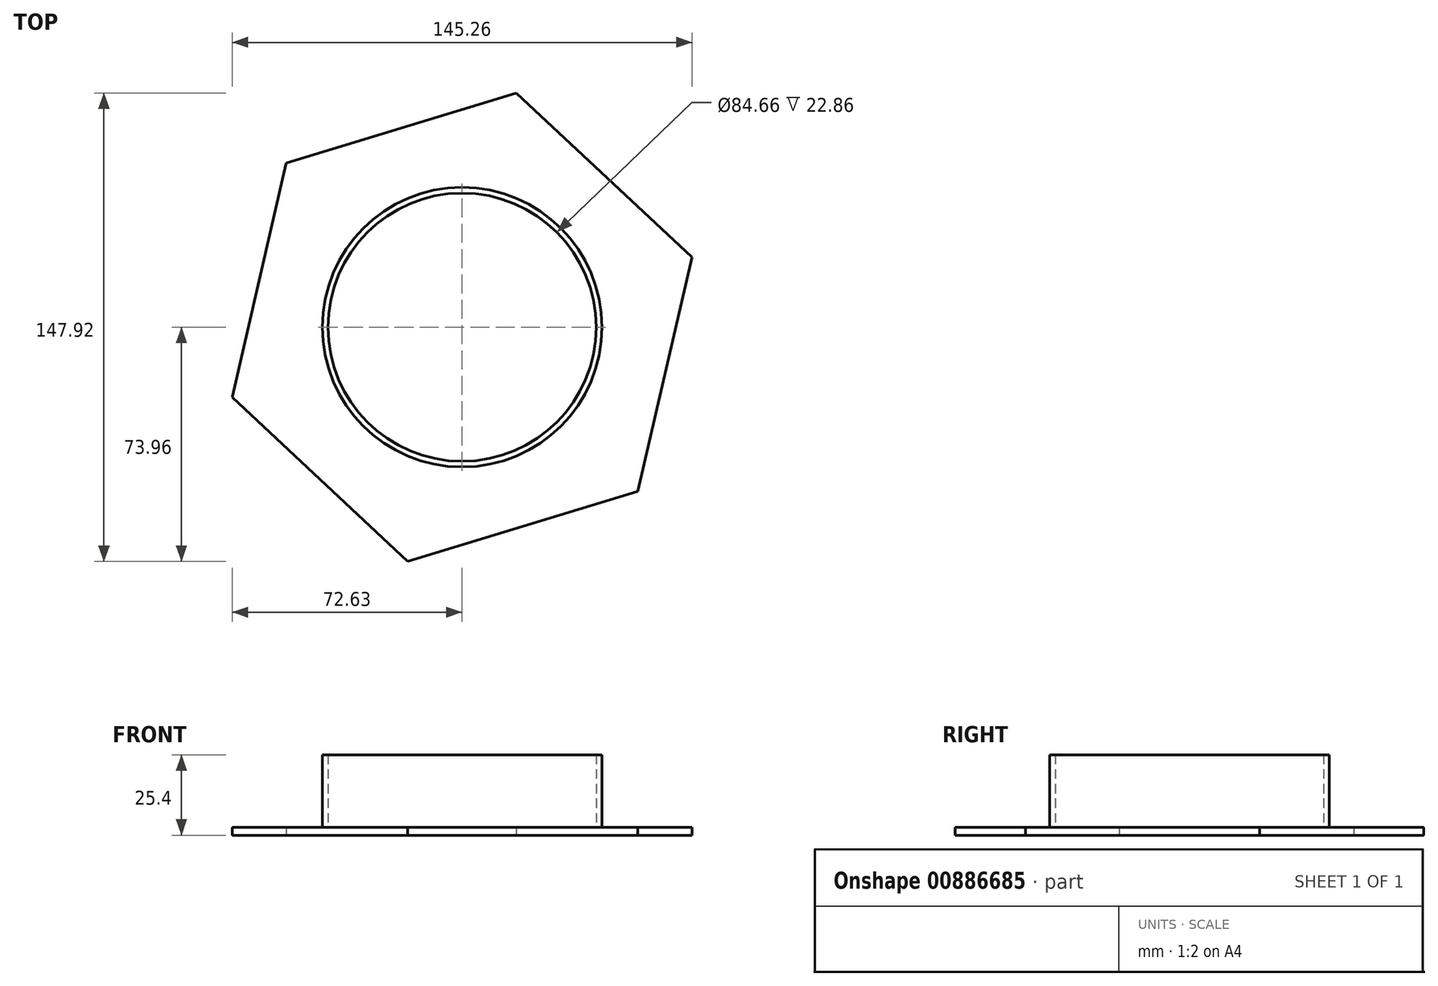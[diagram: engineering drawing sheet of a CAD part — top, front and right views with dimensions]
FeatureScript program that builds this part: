
annotation { "Feature Type Name" : "Feature", "Feature Type Description" : "" }
export const myFeature = defineFeature(function(context is Context, id is Id, definition is map)
    precondition{}
    {
        {
            var Q0;
            Q0=qCreatedBy(makeId("Top.planeOp"),FACE);
            var sketch = newSketch(context, id + "F0", { "sketchPlane" : qUnion([Q0])});
            skCircle(sketch, "E0", {"center": v(0, 0) * mm, "radius": 44.13 * mm});
            skCircle(sketch, "E1", {"center": v(0, 0) * mm, "radius": 42.33 * mm});
            skLineSegment(sketch, "E2", {"start": v(-6.73, 41.8) * mm, "end": v(-6.73, 43.62) * mm});
            skCircle(sketch, "E3", {"center": v(0, 0) * mm, "radius": 38.08 * mm});
            skSolve(sketch);
        }
        {
            var Q0;
            Q0=qCreatedBy(makeId("Top.planeOp"),FACE);
            var sketch = newSketch(context, id + "F1", { "sketchPlane" : qUnion([Q0])});
            skCircle(sketch, "E4.cCircle", {"center": v(0, 0) * mm, "radius": 65.75 * mm, "construction": true});
            skLineSegment(sketch, "E4.0", {"start": v(-55.48, 51.83) * mm, "end": v(17.14, 73.96) * mm});
            skLineSegment(sketch, "E4.1", {"start": v(17.14, 73.96) * mm, "end": v(72.63, 22.14) * mm});
            skLineSegment(sketch, "E4.2", {"start": v(72.63, 22.14) * mm, "end": v(55.48, -51.83) * mm});
            skLineSegment(sketch, "E4.3", {"start": v(55.48, -51.83) * mm, "end": v(-17.14, -73.96) * mm});
            skLineSegment(sketch, "E4.4", {"start": v(-17.14, -73.96) * mm, "end": v(-72.63, -22.14) * mm});
            skLineSegment(sketch, "E4.5", {"start": v(-72.63, -22.14) * mm, "end": v(-55.48, 51.83) * mm});
            skPoint(sketch, "E4.0.midPoint", {"position": v(-19.17, 62.9) * mm});
            skLineSegment(sketch, "E5.bottom", {"start": v(0, 0) * mm, "end": v(0, 0) * mm});
            skLineSegment(sketch, "E5.top", {"start": v(0, 3.15) * mm, "end": v(0, 3.15) * mm});
            skLineSegment(sketch, "E5.left", {"start": v(0, 0) * mm, "end": v(0, 3.15) * mm});
            skLineSegment(sketch, "E5.right", {"start": v(0, 0) * mm, "end": v(0, 3.15) * mm});
            skSolve(sketch);
        }
        {
            var Q0;
            Q0 = qSketchRegion(id + "F0", true);
            extrude(context, id + "F2", {"entities" : qUnion([Q0]), "depth" : 25.4 * mm, "offsetDistance" : 25.4 * mm});
        }
        {
            var Q0;
            Q0 = qSketchRegion(id + "F1", true);
            extrude(context, id + "F3", {"entities" : qUnion([Q0]), "operationType" : NewBodyOperationType.ADD, "depth" : 2.54 * mm, "offsetDistance" : 25.4 * mm});
        }
    });
